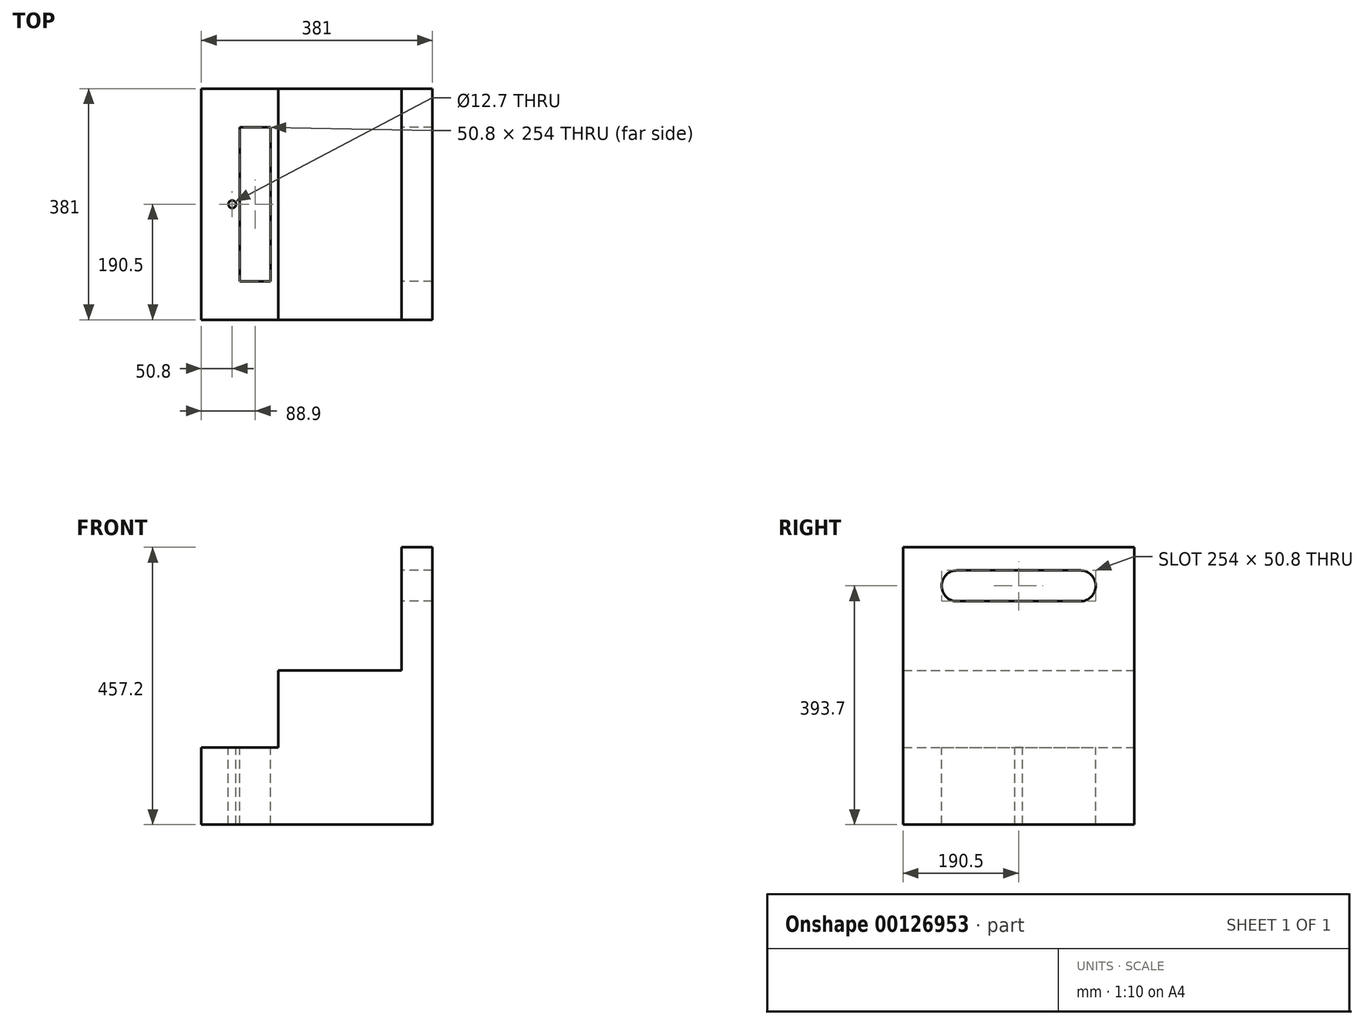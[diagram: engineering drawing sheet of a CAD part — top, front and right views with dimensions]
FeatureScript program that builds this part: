
annotation { "Feature Type Name" : "Feature", "Feature Type Description" : "" }
export const myFeature = defineFeature(function(context is Context, id is Id, definition is map)
    precondition{}
    {
        {
            var Q0;
            Q0=qCreatedBy(makeId("Front.planeOp"),FACE);
            var sketch = newSketch(context, id + "F0", { "sketchPlane" : qUnion([Q0])});
            skLineSegment(sketch, "E0.bottom", {"start": v(190.5, 228.6) * mm, "end": v(139.7, 228.6) * mm});
            skLineSegment(sketch, "E0.top", {"start": v(190.5, -228.6) * mm, "end": v(-190.5, -228.6) * mm});
            skLineSegment(sketch, "E0.left", {"start": v(190.5, 228.6) * mm, "end": v(190.5, -228.6) * mm});
            skLineSegment(sketch, "E0.right", {"start": v(-190.5, -101.6) * mm, "end": v(-190.5, -228.6) * mm});
            skPoint(sketch, "E0.middle", {"position": v(0, 0) * mm});
            skLineSegment(sketch, "E1", {"start": v(139.7, 228.6) * mm, "end": v(139.7, 25.4) * mm});
            skLineSegment(sketch, "E2", {"start": v(139.7, 25.4) * mm, "end": v(-63.5, 25.4) * mm});
            skLineSegment(sketch, "E3", {"start": v(-63.5, 25.4) * mm, "end": v(-63.5, -101.6) * mm});
            skLineSegment(sketch, "E4", {"start": v(-63.5, -101.6) * mm, "end": v(-190.5, -101.6) * mm});
            skPoint(sketch, "E5.orphan", {"position": v(-190.5, 228.6) * mm});
            skSolve(sketch);
        }
        {
            var Q0;
            Q0 = qSketchRegion(id + "F0", true);
            extrude(context, id + "F1", {"entities" : qUnion([Q0]), "depth" : 381 * mm});
        }
        {
            var Q0;
            Q0=makeQuery(id+"F1.opExtrude","SWEPT_FACE",FACE,{"disambiguationData":[OSD([sQuery(id+"F0.wireOp",EDGE,"E4")])]});
            var sketch = newSketch(context, id + "F2", { "sketchPlane" : qUnion([Q0])});
            skCircle(sketch, "E6", {"center": v(-139.7, -190.5) * mm, "radius": 6.35 * mm});
            skSolve(sketch);
        }
        {
            var Q0;
            Q0 = qSketchRegion(id + "F2", true);
            extrude(context, id + "F3", {"entities" : qUnion([Q0]), "operationType" : NewBodyOperationType.REMOVE, "endBound" : BoundingType.THROUGH_ALL, "oppositeDirection" : true, "depth" : 25.4 * mm});
        }
        {
            var Q0;
            Q0=makeQuery(id+"F1.opExtrude","SWEPT_FACE",FACE,{"disambiguationData":[OSD([sQuery(id+"F0.wireOp",EDGE,"E4")])]});
            var sketch = newSketch(context, id + "F4", { "sketchPlane" : qUnion([Q0])});
            skLineSegment(sketch, "E7.bottom", {"start": v(-127, -317.5) * mm, "end": v(-76.2, -317.5) * mm});
            skLineSegment(sketch, "E7.top", {"start": v(-127, -63.5) * mm, "end": v(-76.2, -63.5) * mm});
            skLineSegment(sketch, "E7.left", {"start": v(-127, -317.5) * mm, "end": v(-127, -63.5) * mm});
            skLineSegment(sketch, "E7.right", {"start": v(-76.2, -317.5) * mm, "end": v(-76.2, -63.5) * mm});
            skSolve(sketch);
        }
        {
            var Q0;
            Q0 = qSketchRegion(id + "F4", true);
            extrude(context, id + "F5", {"entities" : qUnion([Q0]), "operationType" : NewBodyOperationType.REMOVE, "endBound" : BoundingType.THROUGH_ALL, "oppositeDirection" : true, "depth" : 25.4 * mm});
        }
        {
            var Q0;
            Q0=makeQuery(id+"F1.opExtrude","SWEPT_FACE",FACE,{"disambiguationData":[OSD([sQuery(id+"F0.wireOp",EDGE,"E1")])]});
            var sketch = newSketch(context, id + "F6", { "sketchPlane" : qUnion([Q0])});
            skLineSegment(sketch, "E8.bottom", {"start": v(292.1, 139.7) * mm, "end": v(88.9, 139.7) * mm});
            skLineSegment(sketch, "E8.top", {"start": v(292.1, 190.5) * mm, "end": v(88.9, 190.5) * mm});
            skArc(sketch, "E9", {"start": v(292.1, 139.7) * mm, "mid": v(317.5, 165.1) * mm, "end": v(292.1, 190.5) * mm});
            skArc(sketch, "E10", {"start": v(88.9, 190.5) * mm, "mid": v(63.5, 165.1) * mm, "end": v(88.9, 139.7) * mm});
            skSolve(sketch);
        }
        {
            var Q0;
            Q0 = qSketchRegion(id + "F6", true);
            extrude(context, id + "F7", {"entities" : qUnion([Q0]), "operationType" : NewBodyOperationType.REMOVE, "oppositeDirection" : true, "depth" : 63.5 * mm});
        }
    });
